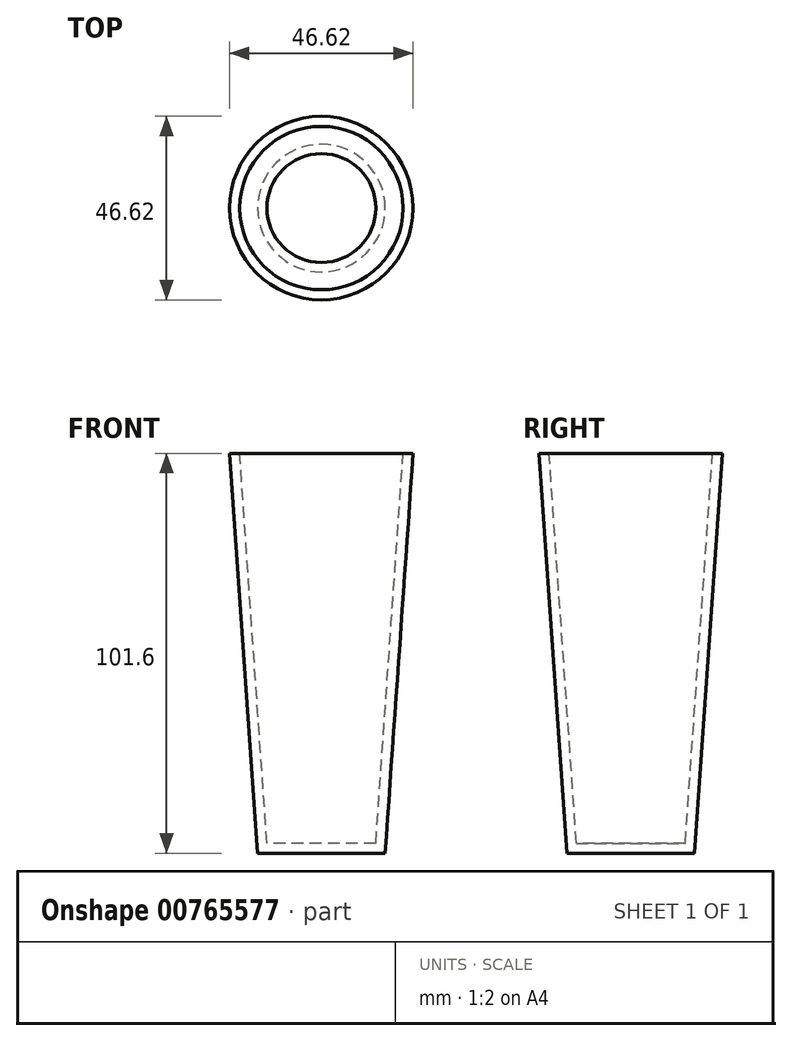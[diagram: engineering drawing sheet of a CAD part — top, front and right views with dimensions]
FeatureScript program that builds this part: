
annotation { "Feature Type Name" : "Feature", "Feature Type Description" : "" }
export const myFeature = defineFeature(function(context is Context, id is Id, definition is map)
    precondition{}
    {
        {
            var Q0;
            Q0=qCreatedBy(makeId("Top.planeOp"),FACE);
            var sketch = newSketch(context, id + "F0", { "sketchPlane" : qUnion([Q0])});
            skCircle(sketch, "E0", {"center": v(0, 0) * mm, "radius": 16.2 * mm});
            skSolve(sketch);
        }
        {
            var Q0;
            Q0 = qSketchRegion(id + "F0", true);
            extrude(context, id + "F1", {"entities" : qUnion([Q0]), "depth" : 101.6 * mm, "offsetDistance" : 25.4 * mm, "hasDraft" : true, "draftAngle" : 4 * degree});
        }
        {
            var Q0;
            Q0=makeQuery(id+"F1.opExtrude","CAP_FACE",FACE,{"disambiguationData":[OSD([sQuery(id+"F0.wireOp",EDGE,"E0")])],"isStart":false});
            shell(context, id + "F2", {"entities" : qUnion([Q0]), "thickness" : 2.54 * mm});
        }
    });
